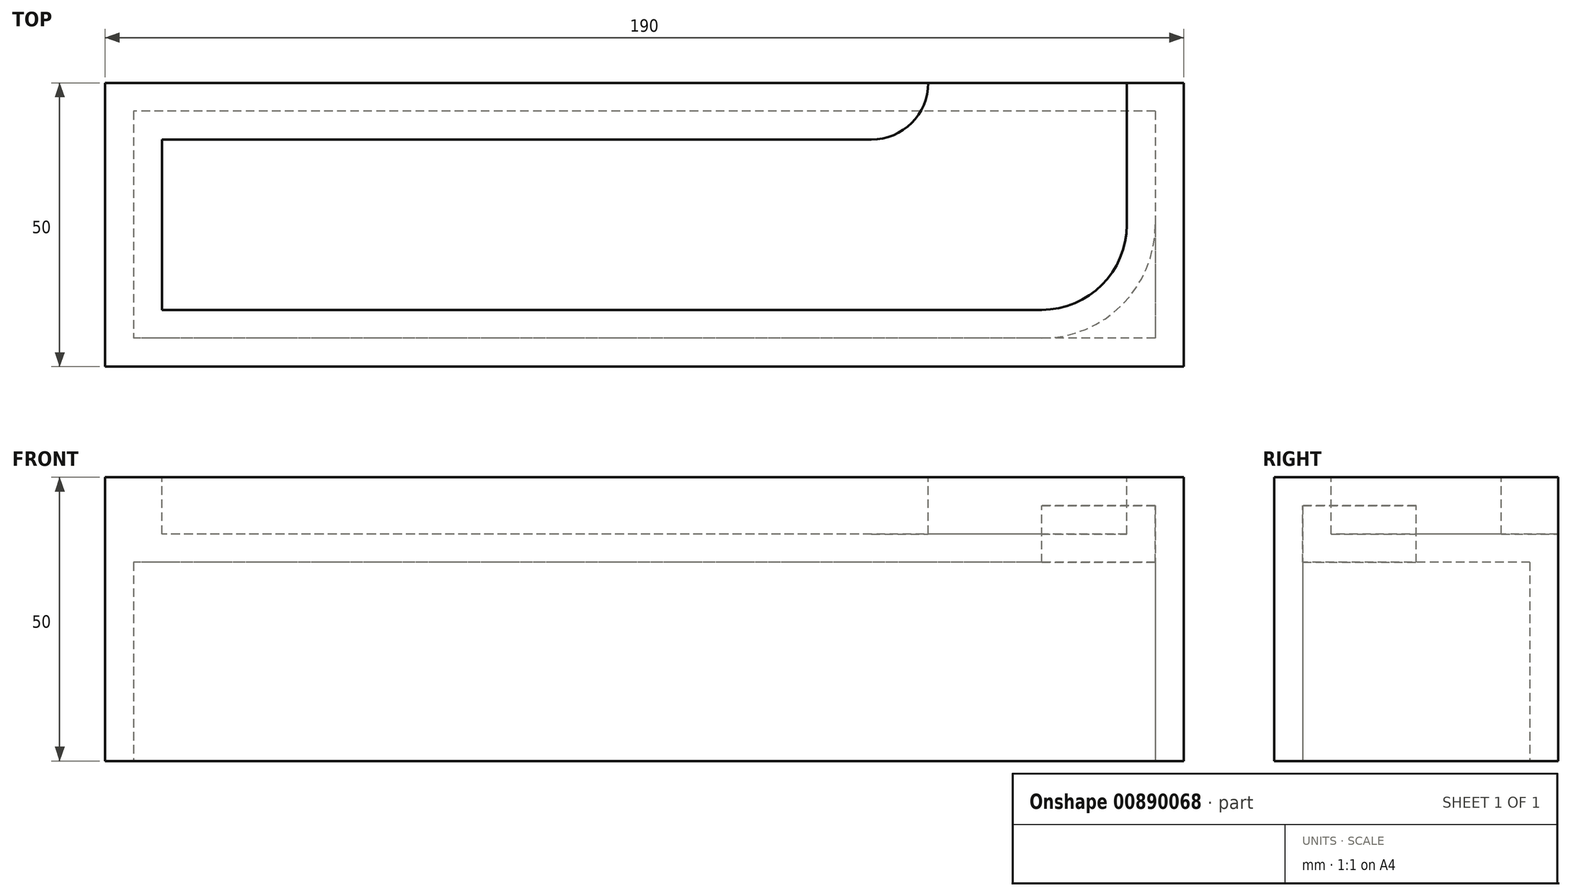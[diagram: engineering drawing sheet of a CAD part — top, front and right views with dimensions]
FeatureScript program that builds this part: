
annotation { "Feature Type Name" : "Feature", "Feature Type Description" : "" }
export const myFeature = defineFeature(function(context is Context, id is Id, definition is map)
    precondition{}
    {
        {
            var Q0;
            Q0=qCreatedBy(makeId("Top.planeOp"),FACE);
            var sketch = newSketch(context, id + "F0", { "sketchPlane" : qUnion([Q0])});
            skLineSegment(sketch, "E0.bottom", {"start": v(95, 25) * mm, "end": v(-95, 25) * mm});
            skLineSegment(sketch, "E0.top", {"start": v(95, -25) * mm, "end": v(-95, -25) * mm});
            skLineSegment(sketch, "E0.left", {"start": v(95, 25) * mm, "end": v(95, -25) * mm});
            skLineSegment(sketch, "E0.right", {"start": v(-95, 25) * mm, "end": v(-95, -25) * mm});
            skPoint(sketch, "E0.middle", {"position": v(0, 0) * mm});
            skSolve(sketch);
        }
        {
            var Q0;
            Q0 = qSketchRegion(id + "F0", true);
            extrude(context, id + "F1", {"entities" : qUnion([Q0]), "depth" : 50 * mm, "offsetDistance" : 25 * mm});
        }
        {
            var Q0;
            Q0=makeQuery(id+"F1.opExtrude","CAP_FACE",FACE,{"disambiguationData":[OSD([sQuery(id+"F0.wireOp",EDGE,"E0.bottom"),sQuery(id+"F0.wireOp",EDGE,"E0.top"),sQuery(id+"F0.wireOp",EDGE,"E0.left"),sQuery(id+"F0.wireOp",EDGE,"E0.right")])],"isStart":false});
            var sketch = newSketch(context, id + "F2", { "sketchPlane" : qUnion([Q0])});
            skLineSegment(sketch, "E1.bottom", {"start": v(40, 15) * mm, "end": v(-85, 15) * mm});
            skLineSegment(sketch, "E1.top", {"start": v(70, -15) * mm, "end": v(-85, -15) * mm});
            skLineSegment(sketch, "E1.left", {"start": v(85, 15) * mm, "end": v(85, 0) * mm});
            skLineSegment(sketch, "E1.right", {"start": v(-85, 15) * mm, "end": v(-85, -15) * mm});
            skPoint(sketch, "E1.middle", {"position": v(0, 0) * mm});
            skArc(sketch, "E2", {"start": v(70, -15) * mm, "mid": v(80.6, -10.6) * mm, "end": v(85, 0) * mm});
            skPoint(sketch, "E3.orphan", {"position": v(85, -15) * mm});
            skArc(sketch, "E4", {"start": v(40, 15) * mm, "mid": v(47.07, 17.93) * mm, "end": v(50, 25) * mm});
            skLineSegment(sketch, "E5", {"start": v(85, 15) * mm, "end": v(85, 25) * mm});
            skLineSegment(sketch, "E6", {"start": v(50, 25) * mm, "end": v(85, 25) * mm});
            skSolve(sketch);
        }
        {
            var Q0;
            Q0 = qSketchRegion(id + "F2", true);
            extrude(context, id + "F3", {"entities" : qUnion([Q0]), "operationType" : NewBodyOperationType.REMOVE, "oppositeDirection" : true, "depth" : 10 * mm, "offsetDistance" : 25 * mm});
        }
        {
            var Q0;
            Q0=makeQuery(id+"F1.opExtrude","CAP_FACE",FACE,{"disambiguationData":[OSD([sQuery(id+"F0.wireOp",EDGE,"E0.bottom"),sQuery(id+"F0.wireOp",EDGE,"E0.top"),sQuery(id+"F0.wireOp",EDGE,"E0.left"),sQuery(id+"F0.wireOp",EDGE,"E0.right")])],"isStart":true});
            shell(context, id + "F4", {"entities" : qUnion([Q0]), "thickness" : 5 * mm});
        }
    });
